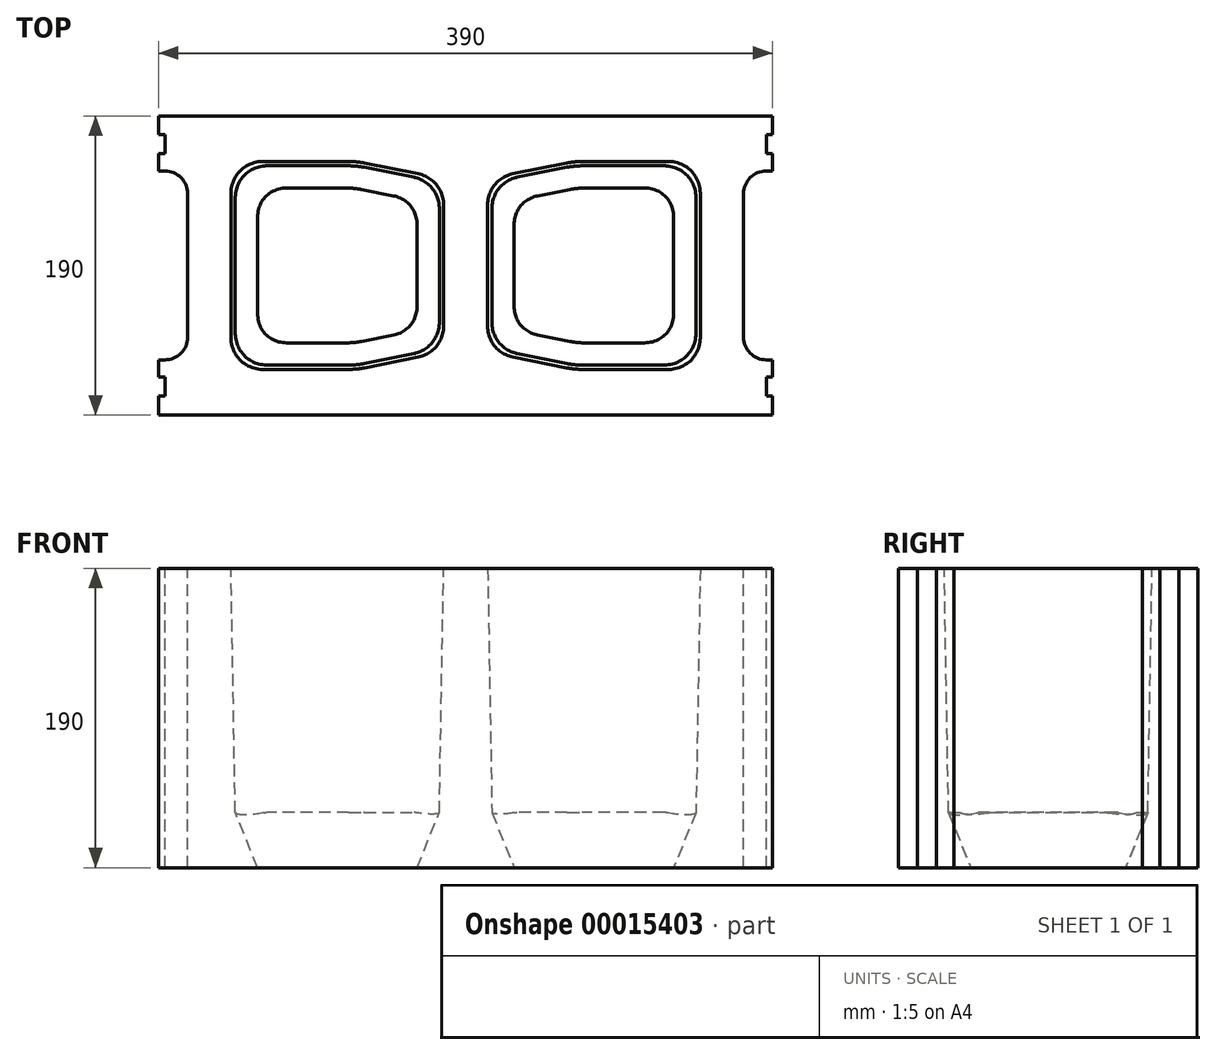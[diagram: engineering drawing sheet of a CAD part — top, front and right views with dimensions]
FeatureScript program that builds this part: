
annotation { "Feature Type Name" : "Feature", "Feature Type Description" : "" }
export const myFeature = defineFeature(function(context is Context, id is Id, definition is map)
    precondition{}
    {
        {
            var Q0;
            Q0=qCreatedBy(makeId("Top.planeOp"),FACE);
            var sketch = newSketch(context, id + "F0", { "sketchPlane" : qUnion([Q0])});
            skLineSegment(sketch, "E0.bottom", {"start": v(-195, 95) * mm, "end": v(195, 95) * mm});
            skLineSegment(sketch, "E0.top", {"start": v(-195, -95) * mm, "end": v(195, -95) * mm});
            skLineSegment(sketch, "E0.left", {"start": v(-195, 95) * mm, "end": v(-195, -95) * mm});
            skLineSegment(sketch, "E0.right", {"start": v(195, 95) * mm, "end": v(195, -95) * mm});
            skSolve(sketch);
        }
        {
            var Q0;
            Q0 = qSketchRegion(id + "F0", true);
            extrude(context, id + "F1", {"entities" : qUnion([Q0]), "depth" : 190 * mm});
        }
        {
            var Q0;
            Q0=makeQuery(id+"F1.opExtrude","CAP_FACE",FACE,{"disambiguationData":[OSD([sQuery(id+"F0.wireOp",EDGE,"E0.bottom"),sQuery(id+"F0.wireOp",EDGE,"E0.top"),sQuery(id+"F0.wireOp",EDGE,"E0.left"),sQuery(id+"F0.wireOp",EDGE,"E0.right")])],"isStart":false});
            var sketch = newSketch(context, id + "F2", { "sketchPlane" : qUnion([Q0])});
            skLineSegment(sketch, "E1.bottom", {"start": v(-195, 83) * mm, "end": v(-191, 83) * mm});
            skLineSegment(sketch, "E1.top", {"start": v(-195, 71) * mm, "end": v(-191, 71) * mm});
            skLineSegment(sketch, "E1.left", {"start": v(-195, 83) * mm, "end": v(-195, 71) * mm});
            skLineSegment(sketch, "E1.right", {"start": v(-191, 83) * mm, "end": v(-191, 71) * mm});
            skSolve(sketch);
        }
        {
            var Q0;
            Q0 = qSketchRegion(id + "F2", true);
            extrude(context, id + "F3", {"entities" : qUnion([Q0]), "operationType" : NewBodyOperationType.REMOVE, "endBound" : BoundingType.THROUGH_ALL, "oppositeDirection" : true, "depth" : 25 * mm});
        }
        {
            var Q0;
            Q0=makeQuery(id+"F1.opExtrude","CAP_FACE",FACE,{"disambiguationData":[OSD([sQuery(id+"F0.wireOp",EDGE,"E0.bottom"),sQuery(id+"F0.wireOp",EDGE,"E0.top"),sQuery(id+"F0.wireOp",EDGE,"E0.left"),sQuery(id+"F0.wireOp",EDGE,"E0.right")])],"isStart":false});
            var sketch = newSketch(context, id + "F4", { "sketchPlane" : qUnion([Q0])});
            skLineSegment(sketch, "E2.bottom", {"start": v(-195, -71) * mm, "end": v(-191, -71) * mm});
            skLineSegment(sketch, "E2.top", {"start": v(-195, -83) * mm, "end": v(-191, -83) * mm});
            skLineSegment(sketch, "E2.left", {"start": v(-195, -71) * mm, "end": v(-195, -83) * mm});
            skLineSegment(sketch, "E2.right", {"start": v(-191, -71) * mm, "end": v(-191, -83) * mm});
            skLineSegment(sketch, "E3.MirrorCS", {"start": v(195, -83) * mm, "end": v(191, -83) * mm});
            skLineSegment(sketch, "E4.MirrorCS", {"start": v(195, -71) * mm, "end": v(191, -71) * mm});
            skLineSegment(sketch, "E5.MirrorCS", {"start": v(191, -71) * mm, "end": v(191, -83) * mm});
            skLineSegment(sketch, "E6.MirrorCS", {"start": v(195, -71) * mm, "end": v(195, -83) * mm});
            skLineSegment(sketch, "E7.MirrorCS", {"start": v(195, 71) * mm, "end": v(191, 71) * mm});
            skLineSegment(sketch, "E8.MirrorCS", {"start": v(191, 71) * mm, "end": v(191, 83) * mm});
            skLineSegment(sketch, "E9.MirrorCS", {"start": v(195, 71) * mm, "end": v(195, 83) * mm});
            skLineSegment(sketch, "E10.MirrorCS", {"start": v(195, 83) * mm, "end": v(191, 83) * mm});
            skSolve(sketch);
        }
        {
            var Q0;
            Q0 = qSketchRegion(id + "F4", true);
            extrude(context, id + "F5", {"entities" : qUnion([Q0]), "operationType" : NewBodyOperationType.REMOVE, "endBound" : BoundingType.THROUGH_ALL, "oppositeDirection" : true, "depth" : 25 * mm});
        }
        {
            var Q0;
            Q0=makeQuery(id+"F1.opExtrude","CAP_FACE",FACE,{"disambiguationData":[OSD([sQuery(id+"F0.wireOp",EDGE,"E0.bottom"),sQuery(id+"F0.wireOp",EDGE,"E0.top"),sQuery(id+"F0.wireOp",EDGE,"E0.left"),sQuery(id+"F0.wireOp",EDGE,"E0.right")])],"isStart":false});
            var sketch = newSketch(context, id + "F6", { "sketchPlane" : qUnion([Q0])});
            skLineSegment(sketch, "E11.bottom", {"start": v(-195, 60) * mm, "end": v(-176.5, 60) * mm});
            skLineSegment(sketch, "E11.top", {"start": v(-195, -60) * mm, "end": v(-176.5, -60) * mm});
            skLineSegment(sketch, "E11.left", {"start": v(-195, 60) * mm, "end": v(-195, -60) * mm});
            skLineSegment(sketch, "E11.right", {"start": v(-176.5, 60) * mm, "end": v(-176.5, -60) * mm});
            skLineSegment(sketch, "E12.MirrorCS", {"start": v(195, 60) * mm, "end": v(176.5, 60) * mm});
            skLineSegment(sketch, "E13.MirrorCS", {"start": v(195, -60) * mm, "end": v(176.5, -60) * mm});
            skLineSegment(sketch, "E14.MirrorCS", {"start": v(195, 60) * mm, "end": v(195, -60) * mm});
            skLineSegment(sketch, "E15.MirrorCS", {"start": v(176.5, 60) * mm, "end": v(176.5, -60) * mm});
            skSolve(sketch);
        }
        {
            var Q0;
            Q0=makeQuery(id+"F6.imprint","IMPRINT",FACE,{"disambiguationData":[TD([[makeQuery(id+"F6.imprint","IMPRINT",EDGE,{"derivedFrom":sQuery(id+"F6.wireOp",EDGE,"E12.MirrorCS")}),1.0]])]});
            var Q1;
            Q1=makeQuery(id+"F6.imprint","IMPRINT",FACE,{"disambiguationData":[TD([[makeQuery(id+"F6.imprint","IMPRINT",EDGE,{"derivedFrom":sQuery(id+"F6.wireOp",EDGE,"E11.bottom")}),-1.0]])]});
            extrude(context, id + "F7", {"entities" : qUnion([Q0, Q1]), "operationType" : NewBodyOperationType.REMOVE, "endBound" : BoundingType.THROUGH_ALL, "oppositeDirection" : true, "depth" : 25 * mm});
        }
        {
            var Q0;
            Q0=makeQuery(id+"F7.boolean.opBoolean","COPY",EDGE,{"derivedFrom":makeQuery(id+"F7.opExtrude","SWEPT_EDGE",EDGE,{"disambiguationData":[OSD([sQuery(id+"F6.wireOp",EDGE,"E11.top"),sQuery(id+"F6.wireOp",EDGE,"E11.right")])]})});
            var Q1;
            Q1=makeQuery(id+"F7.boolean.opBoolean","COPY",EDGE,{"derivedFrom":makeQuery(id+"F7.opExtrude","SWEPT_EDGE",EDGE,{"disambiguationData":[OSD([sQuery(id+"F6.wireOp",EDGE,"E13.MirrorCS"),sQuery(id+"F6.wireOp",EDGE,"E15.MirrorCS")])]})});
            var Q2;
            Q2=makeQuery(id+"F7.boolean.opBoolean","COPY",EDGE,{"derivedFrom":makeQuery(id+"F7.opExtrude","SWEPT_EDGE",EDGE,{"disambiguationData":[OSD([sQuery(id+"F6.wireOp",EDGE,"E12.MirrorCS"),sQuery(id+"F6.wireOp",EDGE,"E15.MirrorCS")])]})});
            var Q3;
            Q3=makeQuery(id+"F7.boolean.opBoolean","COPY",EDGE,{"derivedFrom":makeQuery(id+"F7.opExtrude","SWEPT_EDGE",EDGE,{"disambiguationData":[OSD([sQuery(id+"F6.wireOp",EDGE,"E11.bottom"),sQuery(id+"F6.wireOp",EDGE,"E11.right")])]})});
            fillet(context, id + "F8", {"entities" : qUnion([Q0, Q1, Q2, Q3]), "radius" : 14.5 * mm, "tangentPropagation" : true, "allowEdgeOverflow" : false});
        }
        {
            var Q0;
            Q0=makeQuery(id+"F1.opExtrude","CAP_FACE",FACE,{"disambiguationData":[OSD([sQuery(id+"F0.wireOp",EDGE,"E0.bottom"),sQuery(id+"F0.wireOp",EDGE,"E0.top"),sQuery(id+"F0.wireOp",EDGE,"E0.left"),sQuery(id+"F0.wireOp",EDGE,"E0.right")])],"isStart":false});
            var sketch = newSketch(context, id + "F9", { "sketchPlane" : qUnion([Q0])});
            skLineSegment(sketch, "E16", {"start": v(-149, 66) * mm, "end": v(-149, -66) * mm});
            skLineSegment(sketch, "E17", {"start": v(-149, -66) * mm, "end": v(-69, -66) * mm});
            skLineSegment(sketch, "E18", {"start": v(-69, -66) * mm, "end": v(-14, -55) * mm});
            skLineSegment(sketch, "E19", {"start": v(-14, -55) * mm, "end": v(-14, 55) * mm});
            skLineSegment(sketch, "E20", {"start": v(-14, 55) * mm, "end": v(-69, 66) * mm});
            skLineSegment(sketch, "E21", {"start": v(-69, 66) * mm, "end": v(-149, 66) * mm});
            skLineSegment(sketch, "E22.MirrorCS", {"start": v(149, 66) * mm, "end": v(149, -66) * mm});
            skLineSegment(sketch, "E23.MirrorCS", {"start": v(149, -66) * mm, "end": v(69, -66) * mm});
            skLineSegment(sketch, "E24.MirrorCS", {"start": v(69, -66) * mm, "end": v(14, -55) * mm});
            skLineSegment(sketch, "E25.MirrorCS", {"start": v(69, 66) * mm, "end": v(149, 66) * mm});
            skLineSegment(sketch, "E26.MirrorCS", {"start": v(14, 55) * mm, "end": v(69, 66) * mm});
            skLineSegment(sketch, "E27.MirrorCS", {"start": v(14, -55) * mm, "end": v(14, 55) * mm});
            skSolve(sketch);
        }
        {
            var Q0;
            Q0=makeQuery(id+"F9.imprint","IMPRINT",FACE,{"disambiguationData":[TD([[makeQuery(id+"F9.imprint","IMPRINT",EDGE,{"derivedFrom":sQuery(id+"F9.wireOp",EDGE,"E22.MirrorCS")}),-1.0]])]});
            var Q1;
            Q1=makeQuery(id+"F9.imprint","IMPRINT",FACE,{"disambiguationData":[TD([[makeQuery(id+"F9.imprint","IMPRINT",EDGE,{"derivedFrom":sQuery(id+"F9.wireOp",EDGE,"E16")}),1.0]])]});
            extrude(context, id + "F10", {"entities" : qUnion([Q0, Q1]), "operationType" : NewBodyOperationType.REMOVE, "oppositeDirection" : true, "depth" : 155 * mm, "hasDraft" : true, "draftAngle" : 1 * degree, "draftPullDirection" : true});
        }
        {
            var Q0;
            Q0=makeQuery(id+"F10.boolean.opBoolean","COPY",FACE,{"derivedFrom":makeQuery(id+"F10.opExtrude","CAP_FACE",FACE,{"disambiguationData":[OSD([sQuery(id+"F9.wireOp",EDGE,"E22.MirrorCS"),sQuery(id+"F9.wireOp",EDGE,"E23.MirrorCS"),sQuery(id+"F9.wireOp",EDGE,"E24.MirrorCS"),sQuery(id+"F9.wireOp",EDGE,"E25.MirrorCS"),sQuery(id+"F9.wireOp",EDGE,"E26.MirrorCS"),sQuery(id+"F9.wireOp",EDGE,"E27.MirrorCS")])],"isStart":false})});
            extrude(context, id + "F11", {"entities" : qUnion([Q0]), "operationType" : NewBodyOperationType.REMOVE, "endBound" : BoundingType.THROUGH_ALL, "oppositeDirection" : true, "depth" : 25 * mm, "hasDraft" : true, "draftAngle" : 22 * degree, "draftPullDirection" : true});
        }
        {
            var Q0;
            Q0=makeQuery(id+"F10.boolean.opBoolean","COPY",FACE,{"derivedFrom":makeQuery(id+"F10.opExtrude","CAP_FACE",FACE,{"disambiguationData":[OSD([sQuery(id+"F9.wireOp",EDGE,"E16"),sQuery(id+"F9.wireOp",EDGE,"E17"),sQuery(id+"F9.wireOp",EDGE,"E18"),sQuery(id+"F9.wireOp",EDGE,"E19"),sQuery(id+"F9.wireOp",EDGE,"E20"),sQuery(id+"F9.wireOp",EDGE,"E21")])],"isStart":false})});
            extrude(context, id + "F12", {"entities" : qUnion([Q0]), "operationType" : NewBodyOperationType.REMOVE, "endBound" : BoundingType.THROUGH_ALL, "oppositeDirection" : true, "depth" : 25 * mm, "hasDraft" : true, "draftAngle" : 22 * degree, "draftPullDirection" : true});
        }
        {
            var Q0;
            Q0=makeQuery(id+"F10.boolean.opBoolean","COPY",EDGE,{"derivedFrom":makeQuery(id+"F10.opExtrude","SWEPT_EDGE",EDGE,{"disambiguationData":[OSD([sQuery(id+"F9.wireOp",EDGE,"E24.MirrorCS"),sQuery(id+"F9.wireOp",EDGE,"E27.MirrorCS")])]})});
            var Q1;
            Q1=makeQuery(id+"F10.boolean.opBoolean","COPY",EDGE,{"derivedFrom":makeQuery(id+"F10.opExtrude","SWEPT_EDGE",EDGE,{"disambiguationData":[OSD([sQuery(id+"F9.wireOp",EDGE,"E16"),sQuery(id+"F9.wireOp",EDGE,"E17")])]})});
            var Q2;
            Q2=makeQuery(id+"F10.boolean.opBoolean","COPY",EDGE,{"derivedFrom":makeQuery(id+"F10.opExtrude","SWEPT_EDGE",EDGE,{"disambiguationData":[OSD([sQuery(id+"F9.wireOp",EDGE,"E16"),sQuery(id+"F9.wireOp",EDGE,"E21")])]})});
            var Q3;
            Q3=makeQuery(id+"F10.boolean.opBoolean","COPY",EDGE,{"derivedFrom":makeQuery(id+"F10.opExtrude","SWEPT_EDGE",EDGE,{"disambiguationData":[OSD([sQuery(id+"F9.wireOp",EDGE,"E26.MirrorCS"),sQuery(id+"F9.wireOp",EDGE,"E27.MirrorCS")])]})});
            var Q4;
            Q4=makeQuery(id+"F10.boolean.opBoolean","COPY",EDGE,{"derivedFrom":makeQuery(id+"F10.opExtrude","SWEPT_EDGE",EDGE,{"disambiguationData":[OSD([sQuery(id+"F9.wireOp",EDGE,"E18"),sQuery(id+"F9.wireOp",EDGE,"E19")])]})});
            var Q5;
            Q5=makeQuery(id+"F10.boolean.opBoolean","COPY",EDGE,{"derivedFrom":makeQuery(id+"F10.opExtrude","SWEPT_EDGE",EDGE,{"disambiguationData":[OSD([sQuery(id+"F9.wireOp",EDGE,"E22.MirrorCS"),sQuery(id+"F9.wireOp",EDGE,"E23.MirrorCS")])]})});
            var Q6;
            Q6=makeQuery(id+"F10.boolean.opBoolean","COPY",EDGE,{"derivedFrom":makeQuery(id+"F10.opExtrude","SWEPT_EDGE",EDGE,{"disambiguationData":[OSD([sQuery(id+"F9.wireOp",EDGE,"E22.MirrorCS"),sQuery(id+"F9.wireOp",EDGE,"E25.MirrorCS")])]})});
            var Q7;
            Q7=makeQuery(id+"F10.boolean.opBoolean","COPY",EDGE,{"derivedFrom":makeQuery(id+"F10.opExtrude","SWEPT_EDGE",EDGE,{"disambiguationData":[OSD([sQuery(id+"F9.wireOp",EDGE,"E19"),sQuery(id+"F9.wireOp",EDGE,"E20")])]})});
            var Q8;
            Q8=makeQuery(id+"F12.boolean.opBoolean","COPY",EDGE,{"derivedFrom":makeQuery(id+"F12.opExtrude","SWEPT_EDGE",EDGE,{"disambiguationData":[OSD([sQuery(id+"F9.wireOp",EDGE,"E19"),sQuery(id+"F9.wireOp",EDGE,"E20")])]})});
            var Q9;
            Q9=makeQuery(id+"F11.boolean.opBoolean","COPY",EDGE,{"derivedFrom":makeQuery(id+"F11.opExtrude","SWEPT_EDGE",EDGE,{"disambiguationData":[OSD([sQuery(id+"F9.wireOp",EDGE,"E22.MirrorCS"),sQuery(id+"F9.wireOp",EDGE,"E25.MirrorCS")])]})});
            var Q10;
            Q10=makeQuery(id+"F11.boolean.opBoolean","COPY",EDGE,{"derivedFrom":makeQuery(id+"F11.opExtrude","SWEPT_EDGE",EDGE,{"disambiguationData":[OSD([sQuery(id+"F9.wireOp",EDGE,"E26.MirrorCS"),sQuery(id+"F9.wireOp",EDGE,"E27.MirrorCS")])]})});
            var Q11;
            Q11=makeQuery(id+"F12.boolean.opBoolean","COPY",EDGE,{"derivedFrom":makeQuery(id+"F12.opExtrude","SWEPT_EDGE",EDGE,{"disambiguationData":[OSD([sQuery(id+"F9.wireOp",EDGE,"E16"),sQuery(id+"F9.wireOp",EDGE,"E21")])]})});
            var Q12;
            Q12=makeQuery(id+"F11.boolean.opBoolean","COPY",EDGE,{"derivedFrom":makeQuery(id+"F11.opExtrude","SWEPT_EDGE",EDGE,{"disambiguationData":[OSD([sQuery(id+"F9.wireOp",EDGE,"E22.MirrorCS"),sQuery(id+"F9.wireOp",EDGE,"E23.MirrorCS")])]})});
            var Q13;
            Q13=makeQuery(id+"F12.boolean.opBoolean","COPY",EDGE,{"derivedFrom":makeQuery(id+"F12.opExtrude","SWEPT_EDGE",EDGE,{"disambiguationData":[OSD([sQuery(id+"F9.wireOp",EDGE,"E18"),sQuery(id+"F9.wireOp",EDGE,"E19")])]})});
            var Q14;
            Q14=makeQuery(id+"F12.boolean.opBoolean","COPY",EDGE,{"derivedFrom":makeQuery(id+"F12.opExtrude","SWEPT_EDGE",EDGE,{"disambiguationData":[OSD([sQuery(id+"F9.wireOp",EDGE,"E16"),sQuery(id+"F9.wireOp",EDGE,"E17")])]})});
            var Q15;
            Q15=makeQuery(id+"F11.boolean.opBoolean","COPY",EDGE,{"derivedFrom":makeQuery(id+"F11.opExtrude","SWEPT_EDGE",EDGE,{"disambiguationData":[OSD([sQuery(id+"F9.wireOp",EDGE,"E24.MirrorCS"),sQuery(id+"F9.wireOp",EDGE,"E27.MirrorCS")])]})});
            fillet(context, id + "F13", {"entities" : qUnion([Q0, Q1, Q2, Q3, Q4, Q5, Q6, Q7, Q8, Q9, Q10, Q11, Q12, Q13, Q14, Q15]), "radius" : 20 * mm, "tangentPropagation" : true, "allowEdgeOverflow" : false});
        }
        {
            var Q0;
            Q0=makeQuery(id+"F10.boolean.opBoolean","COPY",EDGE,{"derivedFrom":makeQuery(id+"F10.opExtrude","SWEPT_EDGE",EDGE,{"disambiguationData":[OSD([sQuery(id+"F9.wireOp",EDGE,"E23.MirrorCS"),sQuery(id+"F9.wireOp",EDGE,"E24.MirrorCS")])]})});
            var Q1;
            Q1=makeQuery(id+"F11.boolean.opBoolean","COPY",EDGE,{"derivedFrom":makeQuery(id+"F11.opExtrude","SWEPT_EDGE",EDGE,{"disambiguationData":[OSD([sQuery(id+"F9.wireOp",EDGE,"E23.MirrorCS"),sQuery(id+"F9.wireOp",EDGE,"E24.MirrorCS")])]})});
            var Q2;
            Q2=makeQuery(id+"F10.boolean.opBoolean","COPY",EDGE,{"derivedFrom":makeQuery(id+"F10.opExtrude","SWEPT_EDGE",EDGE,{"disambiguationData":[OSD([sQuery(id+"F9.wireOp",EDGE,"E17"),sQuery(id+"F9.wireOp",EDGE,"E18")])]})});
            var Q3;
            Q3=makeQuery(id+"F12.boolean.opBoolean","COPY",EDGE,{"derivedFrom":makeQuery(id+"F12.opExtrude","SWEPT_EDGE",EDGE,{"disambiguationData":[OSD([sQuery(id+"F9.wireOp",EDGE,"E17"),sQuery(id+"F9.wireOp",EDGE,"E18")])]})});
            var Q4;
            Q4=makeQuery(id+"F12.boolean.opBoolean","COPY",EDGE,{"derivedFrom":makeQuery(id+"F12.opExtrude","SWEPT_EDGE",EDGE,{"disambiguationData":[OSD([sQuery(id+"F9.wireOp",EDGE,"E20"),sQuery(id+"F9.wireOp",EDGE,"E21")])]})});
            var Q5;
            Q5=makeQuery(id+"F10.boolean.opBoolean","COPY",EDGE,{"derivedFrom":makeQuery(id+"F10.opExtrude","SWEPT_EDGE",EDGE,{"disambiguationData":[OSD([sQuery(id+"F9.wireOp",EDGE,"E20"),sQuery(id+"F9.wireOp",EDGE,"E21")])]})});
            var Q6;
            Q6=makeQuery(id+"F11.boolean.opBoolean","COPY",EDGE,{"derivedFrom":makeQuery(id+"F11.opExtrude","SWEPT_EDGE",EDGE,{"disambiguationData":[OSD([sQuery(id+"F9.wireOp",EDGE,"E25.MirrorCS"),sQuery(id+"F9.wireOp",EDGE,"E26.MirrorCS")])]})});
            var Q7;
            Q7=makeQuery(id+"F10.boolean.opBoolean","COPY",EDGE,{"derivedFrom":makeQuery(id+"F10.opExtrude","SWEPT_EDGE",EDGE,{"disambiguationData":[OSD([sQuery(id+"F9.wireOp",EDGE,"E25.MirrorCS"),sQuery(id+"F9.wireOp",EDGE,"E26.MirrorCS")])]})});
            fillet(context, id + "F14", {"entities" : qUnion([Q0, Q1, Q2, Q3, Q4, Q5, Q6, Q7]), "radius" : 50 * mm, "tangentPropagation" : true, "allowEdgeOverflow" : false});
        }
    });
